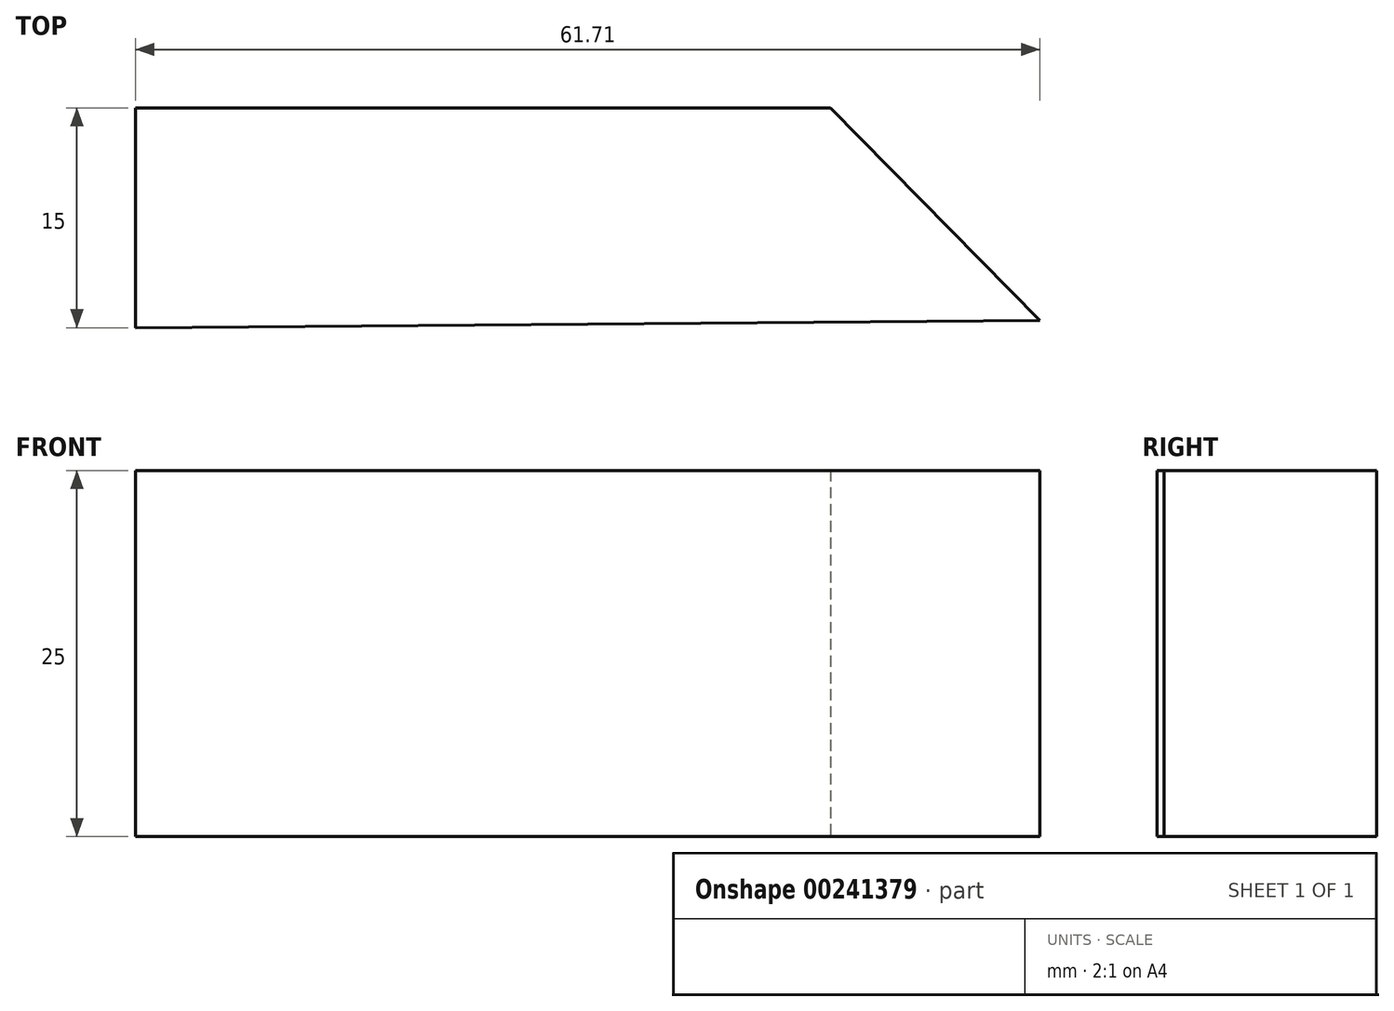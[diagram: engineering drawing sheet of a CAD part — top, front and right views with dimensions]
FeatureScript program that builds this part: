
annotation { "Feature Type Name" : "Feature", "Feature Type Description" : "" }
export const myFeature = defineFeature(function(context is Context, id is Id, definition is map)
    precondition{}
    {
        {
            var Q0;
            Q0=qCreatedBy(makeId("Top.planeOp"),FACE);
            var sketch = newSketch(context, id + "F0", { "sketchPlane" : qUnion([Q0])});
            skLineSegment(sketch, "E0", {"start": v(-23.7, -7.5) * mm, "end": v(-23.7, 7.5) * mm});
            skLineSegment(sketch, "E1", {"start": v(-23.7, 7.5) * mm, "end": v(23.7, 7.5) * mm});
            skLineSegment(sketch, "E2", {"start": v(23.7, 7.5) * mm, "end": v(38, -7) * mm});
            skLineSegment(sketch, "E3", {"start": v(38, -7) * mm, "end": v(-23.7, -7.5) * mm});
            skSolve(sketch);
        }
        {
            var Q0;
            Q0 = qSketchRegion(id + "F0", true);
            extrude(context, id + "F1", {"entities" : qUnion([Q0]), "depth" : 25 * mm});
        }
    });
